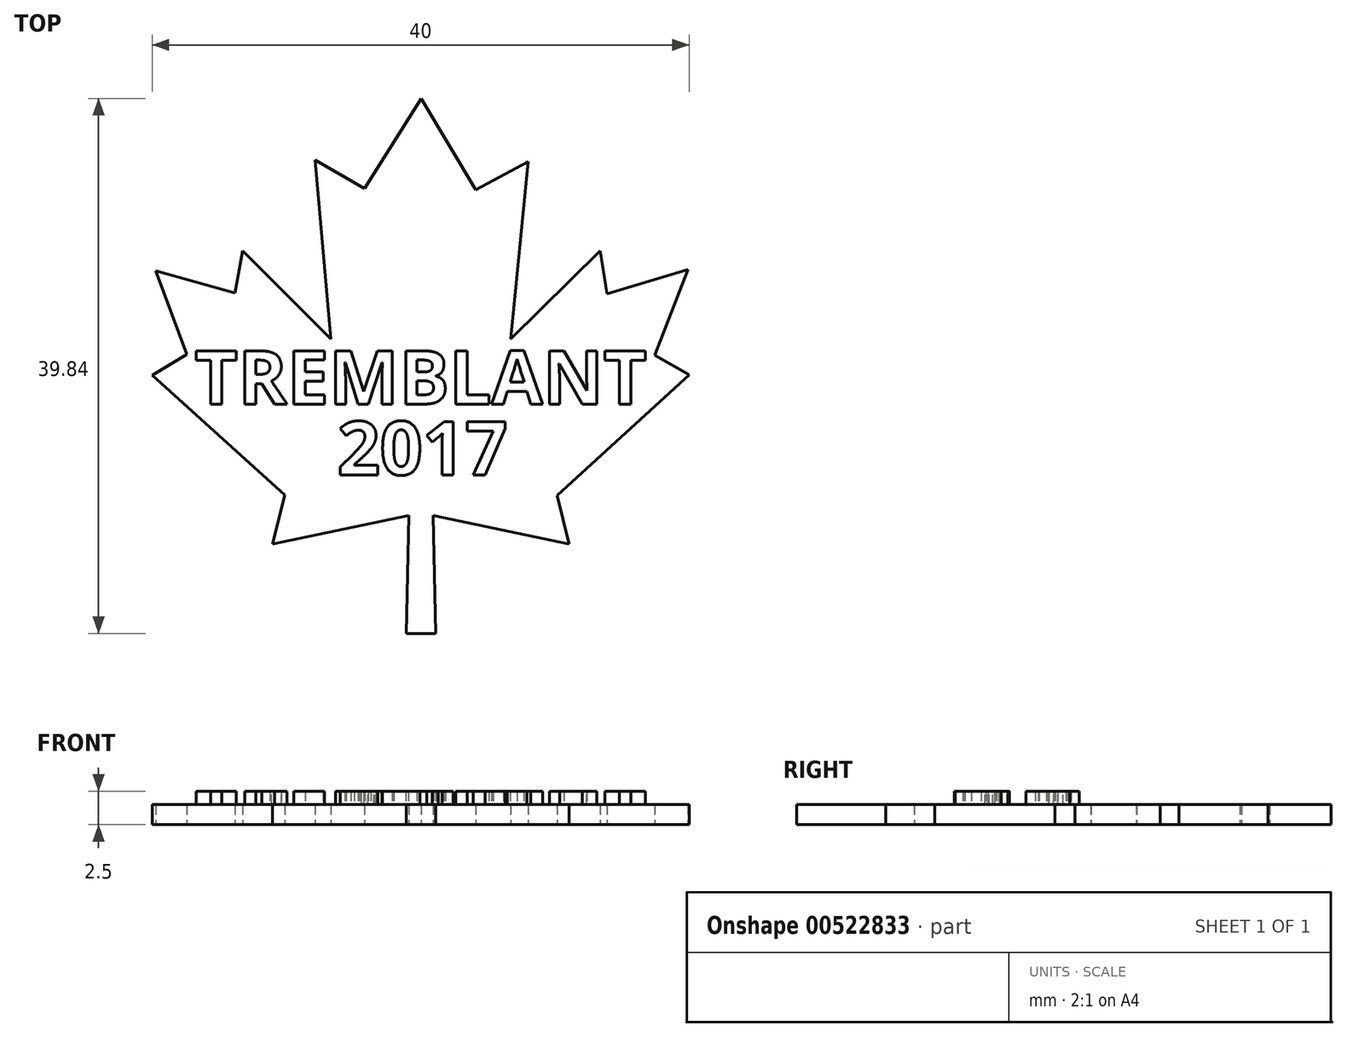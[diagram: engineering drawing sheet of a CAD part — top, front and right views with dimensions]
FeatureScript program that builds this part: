
annotation { "Feature Type Name" : "Feature", "Feature Type Description" : "" }
export const myFeature = defineFeature(function(context is Context, id is Id, definition is map)
    precondition{}
    {
        {
            var Q0;
            Q0=qCreatedBy(makeId("Top.planeOp"),FACE);
            var sketch = newSketch(context, id + "F0", { "sketchPlane" : qUnion([Q0])});
            skLineSegment(sketch, "E0", {"start": v(-20.36, -0.54) * mm, "end": v(-10.47, -9.48) * mm});
            skLineSegment(sketch, "E1", {"start": v(-10.47, -9.48) * mm, "end": v(-11.4, -13.14) * mm});
            skLineSegment(sketch, "E2", {"start": v(-11.4, -13.14) * mm, "end": v(-1.23, -11) * mm});
            skLineSegment(sketch, "E3", {"start": v(-1.23, -11) * mm, "end": v(-1.44, -19.78) * mm});
            skLineSegment(sketch, "E4", {"start": v(-1.44, -19.78) * mm, "end": v(0.77, -19.78) * mm});
            skLineSegment(sketch, "E5", {"start": v(0.77, -19.78) * mm, "end": v(0.55, -11) * mm});
            skLineSegment(sketch, "E6", {"start": v(0.55, -11) * mm, "end": v(10.7, -13.13) * mm});
            skLineSegment(sketch, "E7", {"start": v(10.7, -13.13) * mm, "end": v(9.8, -9.5) * mm});
            skLineSegment(sketch, "E8", {"start": v(9.8, -9.5) * mm, "end": v(19.64, -0.52) * mm});
            skLineSegment(sketch, "E9", {"start": v(19.64, -0.52) * mm, "end": v(17.07, 0.95) * mm});
            skLineSegment(sketch, "E10", {"start": v(17.07, 0.95) * mm, "end": v(19.56, 7.32) * mm});
            skLineSegment(sketch, "E11", {"start": v(19.56, 7.32) * mm, "end": v(13.52, 5.53) * mm});
            skLineSegment(sketch, "E12", {"start": v(13.52, 5.53) * mm, "end": v(13, 8.7) * mm});
            skLineSegment(sketch, "E13", {"start": v(13, 8.7) * mm, "end": v(6.35, 2.14) * mm});
            skLineSegment(sketch, "E14", {"start": v(6.35, 2.14) * mm, "end": v(7.63, 15.35) * mm});
            skLineSegment(sketch, "E15", {"start": v(7.63, 15.35) * mm, "end": v(3.74, 13.25) * mm});
            skLineSegment(sketch, "E16", {"start": v(3.74, 13.25) * mm, "end": v(-0.34, 20.06) * mm});
            skLineSegment(sketch, "E17", {"start": v(-0.34, 20.06) * mm, "end": v(-4.54, 13.36) * mm});
            skLineSegment(sketch, "E18", {"start": v(-4.54, 13.36) * mm, "end": v(-8.24, 15.48) * mm});
            skLineSegment(sketch, "E19", {"start": v(-8.24, 15.48) * mm, "end": v(-7.05, 2.15) * mm});
            skLineSegment(sketch, "E20", {"start": v(-7.05, 2.15) * mm, "end": v(-13.63, 8.7) * mm});
            skLineSegment(sketch, "E21", {"start": v(-13.63, 8.7) * mm, "end": v(-14.19, 5.57) * mm});
            skLineSegment(sketch, "E22", {"start": v(-14.19, 5.57) * mm, "end": v(-20.12, 7.24) * mm});
            skLineSegment(sketch, "E23", {"start": v(-20.12, 7.24) * mm, "end": v(-17.8, 1) * mm});
            skLineSegment(sketch, "E24", {"start": v(-17.8, 1) * mm, "end": v(-20.36, -0.54) * mm});
            skSolve(sketch);
        }
        {
            var Q0;
            Q0 = qSketchRegion(id + "F0", true);
            extrude(context, id + "F1", {"entities" : qUnion([Q0]), "depth" : 1.5 * mm, "offsetDistance" : 25 * mm});
        }
        {
            var Q0;
            Q0=makeQuery(id+"F1.opExtrude","CAP_FACE",FACE,{"disambiguationData":[OSD([sQuery(id+"F0.wireOp",EDGE,"E0"),sQuery(id+"F0.wireOp",EDGE,"E1"),sQuery(id+"F0.wireOp",EDGE,"E2"),sQuery(id+"F0.wireOp",EDGE,"E3"),sQuery(id+"F0.wireOp",EDGE,"E4"),sQuery(id+"F0.wireOp",EDGE,"E5"),sQuery(id+"F0.wireOp",EDGE,"E6"),sQuery(id+"F0.wireOp",EDGE,"E7"),sQuery(id+"F0.wireOp",EDGE,"E8"),sQuery(id+"F0.wireOp",EDGE,"E9"),sQuery(id+"F0.wireOp",EDGE,"E10"),sQuery(id+"F0.wireOp",EDGE,"E11"),sQuery(id+"F0.wireOp",EDGE,"E12"),sQuery(id+"F0.wireOp",EDGE,"E13"),sQuery(id+"F0.wireOp",EDGE,"E14"),sQuery(id+"F0.wireOp",EDGE,"E15"),sQuery(id+"F0.wireOp",EDGE,"E16"),sQuery(id+"F0.wireOp",EDGE,"E17"),sQuery(id+"F0.wireOp",EDGE,"E18"),sQuery(id+"F0.wireOp",EDGE,"E19"),sQuery(id+"F0.wireOp",EDGE,"E20"),sQuery(id+"F0.wireOp",EDGE,"E21"),sQuery(id+"F0.wireOp",EDGE,"E22"),sQuery(id+"F0.wireOp",EDGE,"E23"),sQuery(id+"F0.wireOp",EDGE,"E24")])],"isStart":false});
            var sketch = newSketch(context, id + "F2", { "sketchPlane" : qUnion([Q0])});
            skText(sketch, "E25", { "text": "TREMBLANT", "fontName": "OpenSans-Bold.ttf"});
            skText(sketch, "E26", { "text": "2017", "fontName": "OpenSans-Bold.ttf"});
            const initialGuessF2  = {"E25": [-0.0172, -0.0027, 1, 0, 0.004], "E26": [-0.00657, -0.00797, 1, 0, 0.004]};
            skSetInitialGuess(sketch, initialGuessF2);
            skSolve(sketch);
        }
        {
            var Q0;
            Q0 = qSketchRegion(id + "F2", true);
            extrude(context, id + "F3", {"entities" : qUnion([Q0]), "operationType" : NewBodyOperationType.ADD, "depth" : 1 * mm, "offsetDistance" : 25 * mm});
        }
    });
